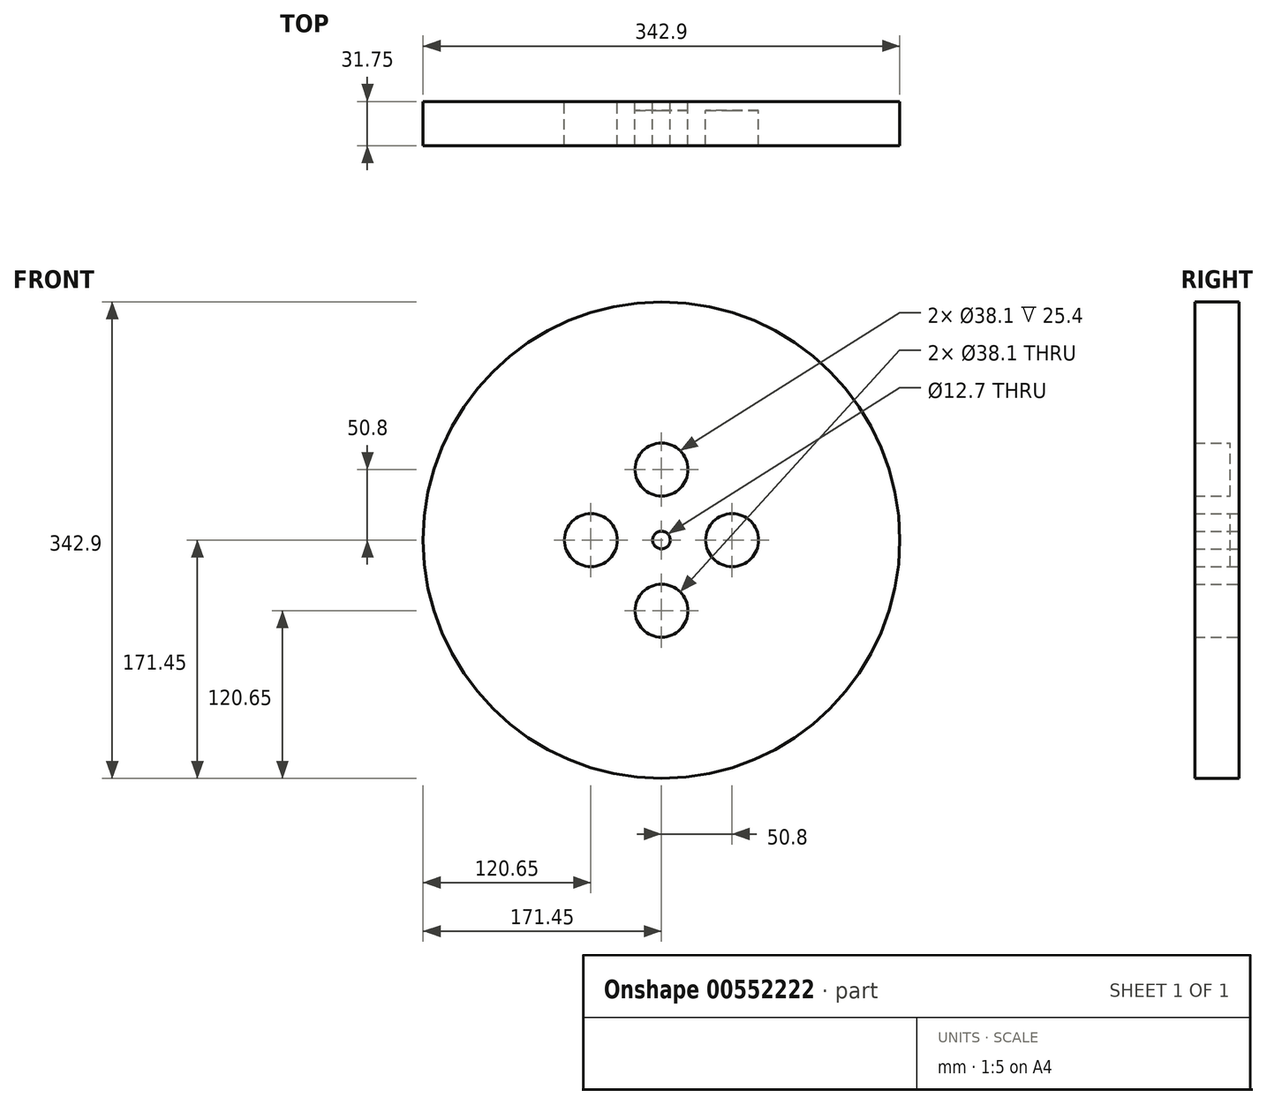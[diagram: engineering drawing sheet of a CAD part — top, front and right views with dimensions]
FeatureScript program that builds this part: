
annotation { "Feature Type Name" : "Feature", "Feature Type Description" : "" }
export const myFeature = defineFeature(function(context is Context, id is Id, definition is map)
    precondition{}
    {
        {
            var Q0;
            Q0=qCreatedBy(makeId("Front.planeOp"),FACE);
            var sketch = newSketch(context, id + "F0", { "sketchPlane" : qUnion([Q0])});
            skCircle(sketch, "E0", {"center": v(0, 0) * mm, "radius": 171.45 * mm});
            skCircle(sketch, "E1", {"center": v(0, 0) * mm, "radius": 50.8 * mm, "construction": true});
            skCircle(sketch, "E2", {"center": v(0, 50.8) * mm, "radius": 19.05 * mm});
            skCircle(sketch, "E3.MirrorC", {"center": v(0, -50.8) * mm, "radius": 19.05 * mm});
            skCircle(sketch, "E4", {"center": v(50.8, 0) * mm, "radius": 19.05 * mm});
            skCircle(sketch, "E5.MirrorC", {"center": v(-50.8, 0) * mm, "radius": 19.05 * mm});
            skCircle(sketch, "E6", {"center": v(0, 0) * mm, "radius": 6.35 * mm});
            skSolve(sketch);
        }
        {
            var Q0;
            Q0=makeQuery(id+"F0.imprint","IMPRINT",FACE,{"disambiguationData":[TD([[makeQuery(id+"F0.imprint","IMPRINT",EDGE,{"derivedFrom":sQuery(id+"F0.wireOp",EDGE,"E0")}),1.0]])]});
            extrude(context, id + "F1", {"entities" : qUnion([Q0]), "depth" : 31.75 * mm, "offsetDistance" : 25.4 * mm});
        }
        {
            var Q0;
            Q0=makeQuery(id+"F0.imprint","IMPRINT",FACE,{"disambiguationData":[TD([[makeQuery(id+"F0.imprint","IMPRINT",EDGE,{"derivedFrom":sQuery(id+"F0.wireOp",EDGE,"E2")}),1.0]])]});
            var Q1;
            Q1=makeQuery(id+"F0.imprint","IMPRINT",FACE,{"disambiguationData":[TD([[makeQuery(id+"F0.imprint","IMPRINT",EDGE,{"derivedFrom":sQuery(id+"F0.wireOp",EDGE,"E4")}),1.0]])]});
            var Q2;
            Q2=makeQuery(id+"F0.imprint","IMPRINT",FACE,{"disambiguationData":[TD([[makeQuery(id+"F0.imprint","IMPRINT",EDGE,{"derivedFrom":sQuery(id+"F0.wireOp",EDGE,"E5.MirrorC")}),-1.0]])]});
            var Q3;
            Q3=makeQuery(id+"F0.imprint","IMPRINT",FACE,{"disambiguationData":[TD([[makeQuery(id+"F0.imprint","IMPRINT",EDGE,{"derivedFrom":sQuery(id+"F0.wireOp",EDGE,"E3.MirrorC")}),-1.0]])]});
            extrude(context, id + "F2", {"entities" : qUnion([Q0, Q1, Q2, Q3]), "operationType" : NewBodyOperationType.ADD, "depth" : 6.35 * mm, "offsetDistance" : 25.4 * mm});
        }
    });
